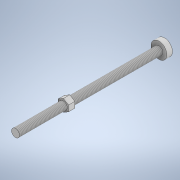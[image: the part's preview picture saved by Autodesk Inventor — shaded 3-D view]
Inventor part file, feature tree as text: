
AUTODESK INVENTOR PART (.ipt)
format: ipt  version: 2020 (Build 240168000, 168)  size: 119,808 bytes
history: native  units: in
note: dims shown in document units (in); Inventor stores cm internally (conversion verified against a paired STEP export)
features: extrude x3, sketch x2, thread x1, plane x1
ambient origin geometry x8: Origin, YZ Plane, XZ Plane, XY Plane, X Axis, Y Axis, Z Axis, Center Point
bodies: Body1 (feature_tree)
feature tree (7):
  extrude  "Extrusion3"  Depth=0.1969in
  extrude  "Extrusion4"  Depth=0.3937in
  thread  "Thread2"  [1 undecoded]
  plane  "Work Plane1"
  extrude  "Extrusion5"  Depth=3.5433in TaperAngle=0.0deg
  sketch  "Sketch4"  dims[d16=3.5433in d17=0.0in d18=0.3937in d19=0.1378in d20=0.0in d21=3.5433in d22=0.0in d23=-1.1811in d24=0.1575in d25=0.0in]
  sketch  "Sketch3"  dims[d12=0.1969in d14=0.1969in d15=0.2953in]
note: 1 required parameter value undecoded (feature->parameter linkage not recoverable at this tier; creation-order binding heuristic only, values carry confidence <= 0.55)
